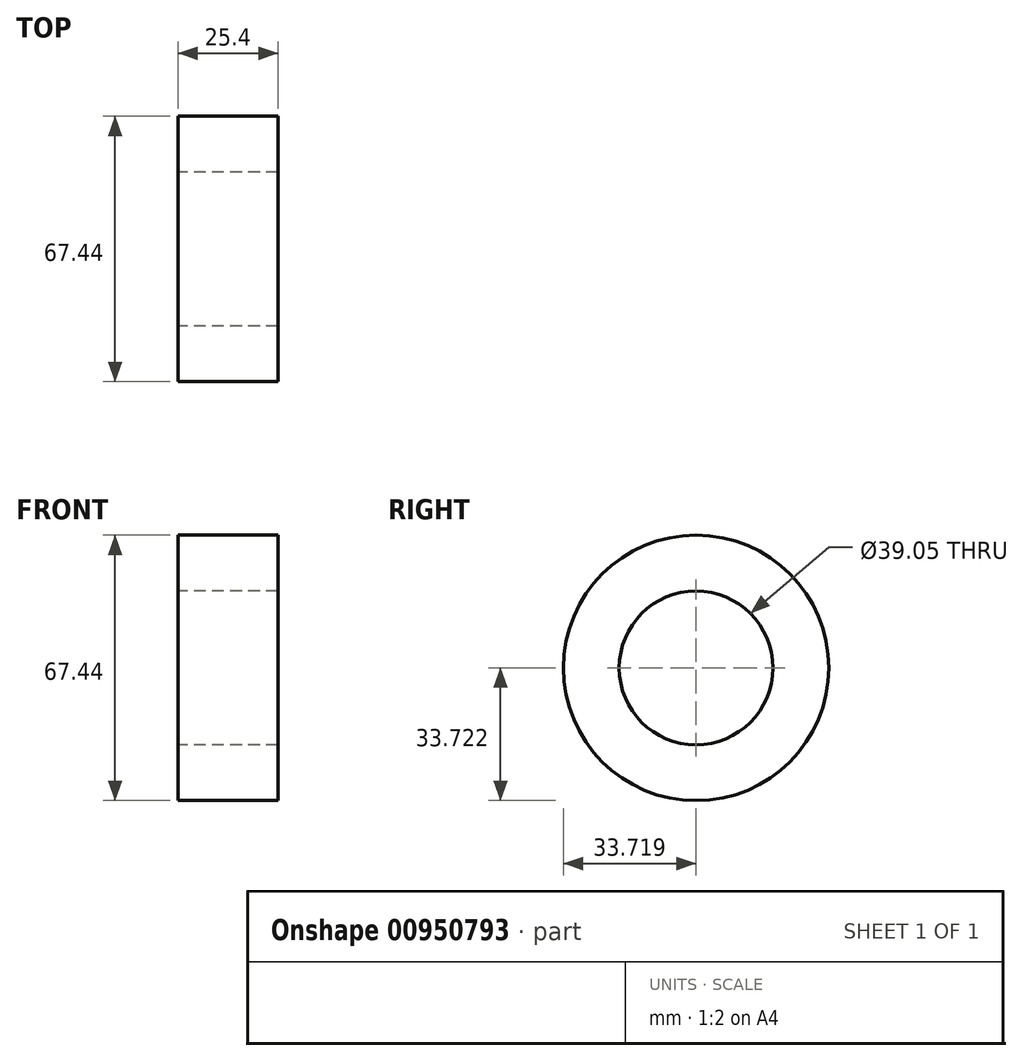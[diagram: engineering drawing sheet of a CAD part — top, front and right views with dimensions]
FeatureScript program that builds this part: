
annotation { "Feature Type Name" : "Feature", "Feature Type Description" : "" }
export const myFeature = defineFeature(function(context is Context, id is Id, definition is map)
    precondition{}
    {
        {
            var Q0;
            Q0=qCreatedBy(makeId("Right.planeOp"),FACE);
            var sketch = newSketch(context, id + "F0", { "sketchPlane" : qUnion([Q0])});
            skCircle(sketch, "E0", {"center": v(-45.7, 48.71) * mm, "radius": 19.53 * mm});
            skCircle(sketch, "E1", {"center": v(-45.7, 48.71) * mm, "radius": 33.72 * mm});
            skSolve(sketch);
        }
        {
            var Q0;
            Q0=makeQuery(id+"F0.imprint","IMPRINT",FACE,{"disambiguationData":[TD([[makeQuery(id+"F0.imprint","IMPRINT",EDGE,{"derivedFrom":sQuery(id+"F0.wireOp",EDGE,"E0")}),-1.0]])]});
            extrude(context, id + "F1", {"entities" : qUnion([Q0]), "depth" : 25.4 * mm, "offsetDistance" : 25.4 * mm});
        }
    });
